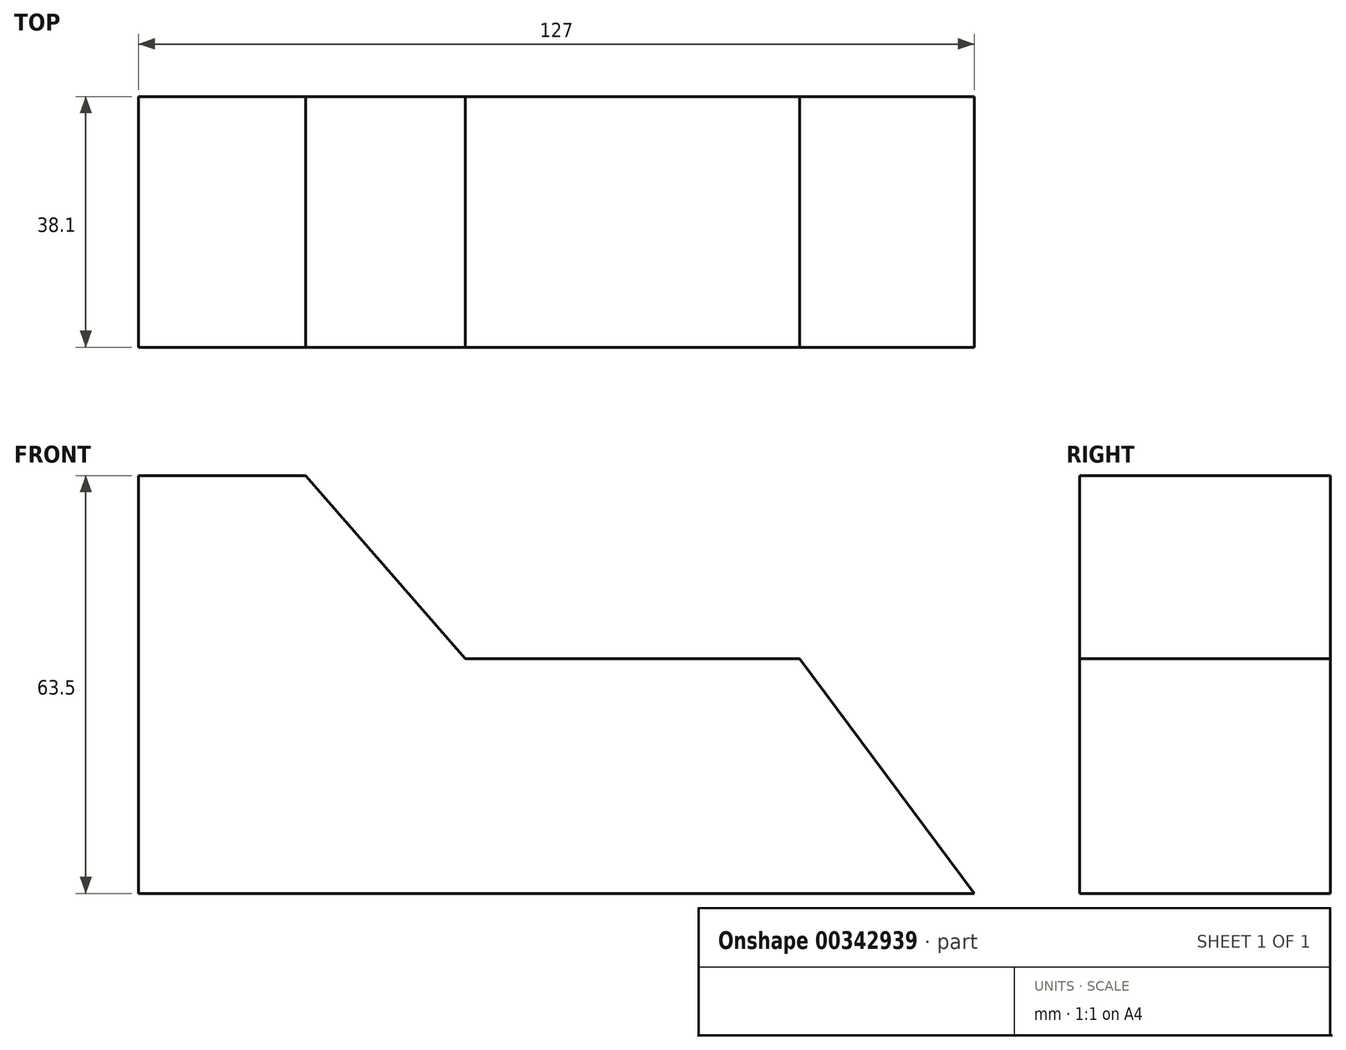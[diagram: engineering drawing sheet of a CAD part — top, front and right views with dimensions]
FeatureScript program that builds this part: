
annotation { "Feature Type Name" : "Feature", "Feature Type Description" : "" }
export const myFeature = defineFeature(function(context is Context, id is Id, definition is map)
    precondition{}
    {
        {
            var Q0;
            Q0=qCreatedBy(makeId("Front.planeOp"),FACE);
            var sketch = newSketch(context, id + "F0", { "sketchPlane" : qUnion([Q0])});
            skLineSegment(sketch, "E0", {"start": v(-58.5, 45.54) * mm, "end": v(-58.5, -17.96) * mm});
            skLineSegment(sketch, "E1", {"start": v(-58.5, -17.96) * mm, "end": v(68.5, -17.96) * mm});
            skLineSegment(sketch, "E2", {"start": v(-58.5, 45.54) * mm, "end": v(-33.1, 45.54) * mm});
            skLineSegment(sketch, "E3", {"start": v(68.5, -17.96) * mm, "end": v(41.96, 17.7) * mm});
            skLineSegment(sketch, "E4", {"start": v(41.96, 17.7) * mm, "end": v(-8.84, 17.7) * mm});
            skLineSegment(sketch, "E5", {"start": v(-33.1, 45.54) * mm, "end": v(-8.84, 17.7) * mm});
            skSolve(sketch);
        }
        {
            var Q0;
            Q0 = qSketchRegion(id + "F0", true);
            extrude(context, id + "F1", {"entities" : qUnion([Q0]), "depth" : 38.1 * mm});
        }
    });
